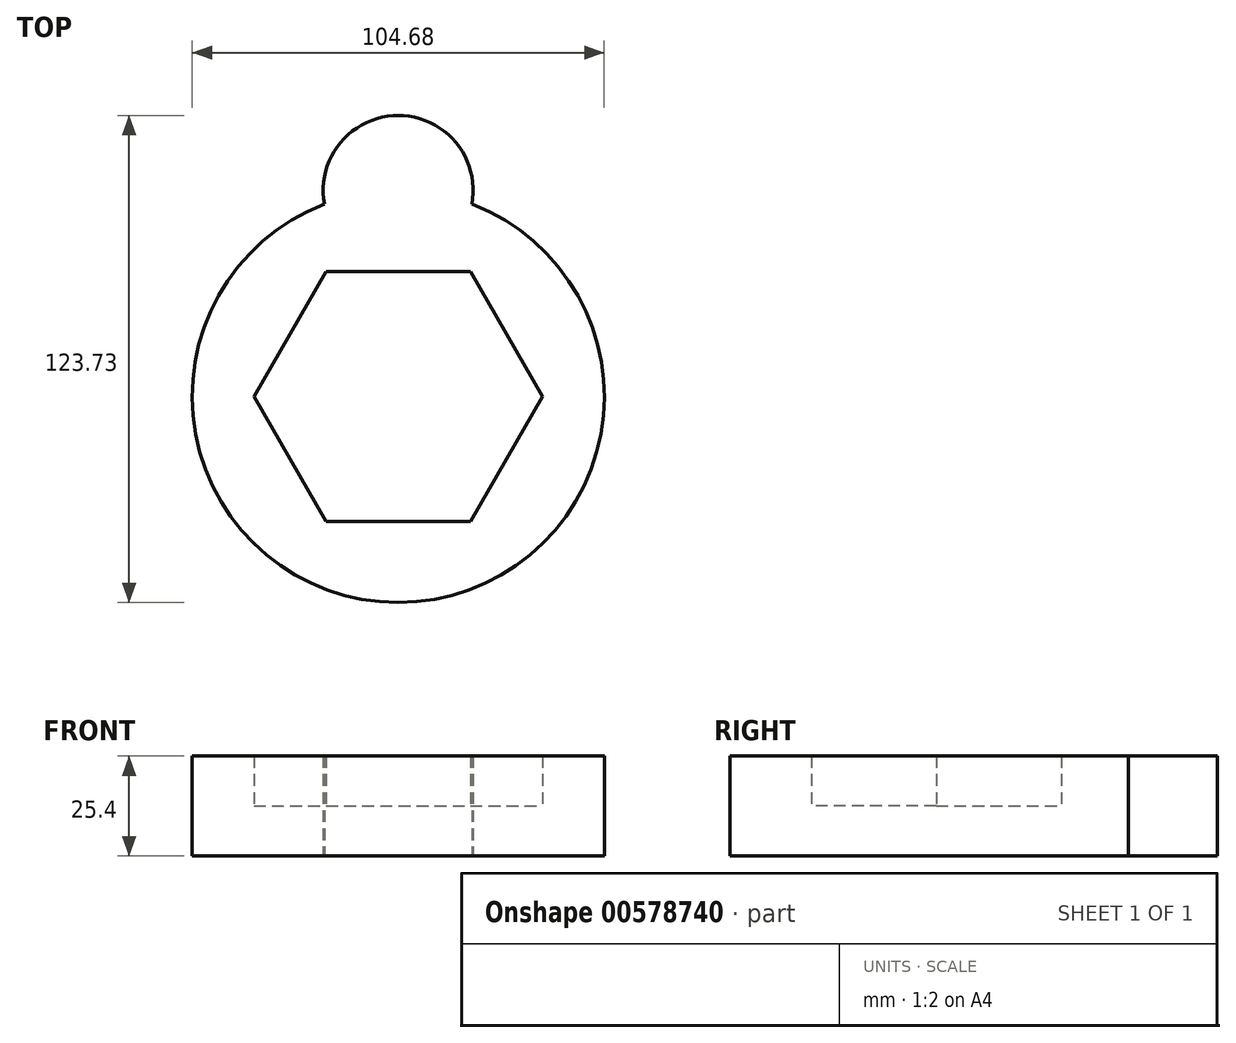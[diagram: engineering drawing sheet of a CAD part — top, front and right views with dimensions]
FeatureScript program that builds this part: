
annotation { "Feature Type Name" : "Feature", "Feature Type Description" : "" }
export const myFeature = defineFeature(function(context is Context, id is Id, definition is map)
    precondition{}
    {
        {
            var Q0;
            Q0=qCreatedBy(makeId("Top.planeOp"),FACE);
            var sketch = newSketch(context, id + "F0", { "sketchPlane" : qUnion([Q0])});
            skCircle(sketch, "E0.cCircle", {"center": v(0, 0) * mm, "radius": 31.75 * mm, "construction": true});
            skLineSegment(sketch, "E0.0", {"start": v(-18.33, 31.75) * mm, "end": v(18.33, 31.75) * mm});
            skLineSegment(sketch, "E0.1", {"start": v(18.33, 31.75) * mm, "end": v(36.66, 0) * mm});
            skLineSegment(sketch, "E0.2", {"start": v(36.66, 0) * mm, "end": v(18.33, -31.75) * mm});
            skLineSegment(sketch, "E0.3", {"start": v(18.33, -31.75) * mm, "end": v(-18.33, -31.75) * mm});
            skLineSegment(sketch, "E0.4", {"start": v(-18.33, -31.75) * mm, "end": v(-36.66, 0) * mm});
            skLineSegment(sketch, "E0.5", {"start": v(-36.66, 0) * mm, "end": v(-18.33, 31.75) * mm});
            skPoint(sketch, "E0.0.midPoint", {"position": v(0, 31.75) * mm});
            skCircle(sketch, "E1", {"center": v(0, 0) * mm, "radius": 52.34 * mm});
            skArc(sketch, "E2", {"start": v(18.73, 48.88) * mm, "mid": v(0, 71.4) * mm, "end": v(-18.73, 48.88) * mm});
            skSolve(sketch);
        }
        {
            var Q0;
            Q0=qSketchRegion(id+"F0",true);
            extrude(context, id + "F1", {"entities" : qUnion([Q0]), "depth" : 25.4 * mm, "offsetDistance" : 25.4 * mm});
        }
        {
            var Q0;
            Q0=makeQuery(id+"F0.imprint","IMPRINT",FACE,{"disambiguationData":[TD([[makeQuery(id+"F0.imprint","IMPRINT",EDGE,{"derivedFrom":sQuery(id+"F0.wireOp",EDGE,"E0.0")}),-1.0]])]});
            extrude(context, id + "F2", {"entities" : qUnion([Q0]), "operationType" : NewBodyOperationType.ADD, "depth" : 12.7 * mm, "offsetDistance" : 25.4 * mm});
        }
    });
